# Revit family: 794BOX1 + 794219-V2
name_source: partatom
category: Plumbing Fixtures
revit_build: Autodesk Revit 2015 (Build: 20140606_1530(x64)
units: mm (PartAtom-declared; Revit-internal decimal feet)

## types (1)
- Type 1
    Category = Shower mixer
    Description = French manufacturer Delabie is a leader in the European sanitary ware market for non-domestic places. Water controls, solutions for disabled people, sanitary ware, for schools, leisure centres, offices, hospitals, airports…
    Diameter = 19 mm  [stored 0.062336 ft]
    Features = Recessed time flow shower kit: Chrome-plated 160 x 160mm vandal proof metal plate. Waterproof recessing housing: - Collar with waterproof seal. - Hydraulic connection from the exterior and maintenance from the front. - Modular installation (rails, load-bearing walls, panels). - Compatible with wall finishes 13 - 120 mm. - Adaptable to standard pipe supply or "pipe in pipe". - Stopcocks and flow rate adjustment, filters, non-return valves and integrated cartridge are accessible from the front. - Single control mixer F½" . - Delivery in 2 kits: safe network purge without sensitive elements. Operation and temperature adjustment via push-button. Maximum temperature limiter (can be adjusted by installer). Time flow ~30 sec., can be adjusted. Soft-touch operation. Flow rate 6 lpm at 3 bar. Chrome-plated, tamperproof ROUND shower head with scale-resistant nozzle and automatic flow rate regulation.
    Finish = Chrome-plated
    FlowRate = 6 lpm at 3 bar
    H = 600 mm  [stored 1.9685 ft]
    IntegralAccessoryOptions = Thermostatic mixing valve
    Manufacturer = DELABIE
    ManufacturerName = DELABIE
    Material = Metal
    Model = TEMPOMIX 3
    Model number = 794BOX1 + 794219
    Name = 794BOX1 + 794219
    NominalHeight = 16 cm
    NominalLength = 16 cm
    NominalWidth = 9.3 - 19 cm
    Operation = Single control time flow mixer
    Polantis code = DLB090006
    ProductInformation = http://www.delabie.com
    SerialNumber = 3456330167796 + 3456330167857
    URL = http://www.delabie.com
    WarrantyDescription = Any manufacturing defect
    WarrantyDurationUnit = 10 years
    WaterSupplyTemperatureMaximum = 55°C-85° (∆50°C : CW/HW)

note: [stored X ft] marks values corroborated as IEEE doubles in the binary element streams (Revit-internal decimal feet)

## geometry (parser evidence)
native form markers: Sweep x3
no freeform markers — native parametric forms only
